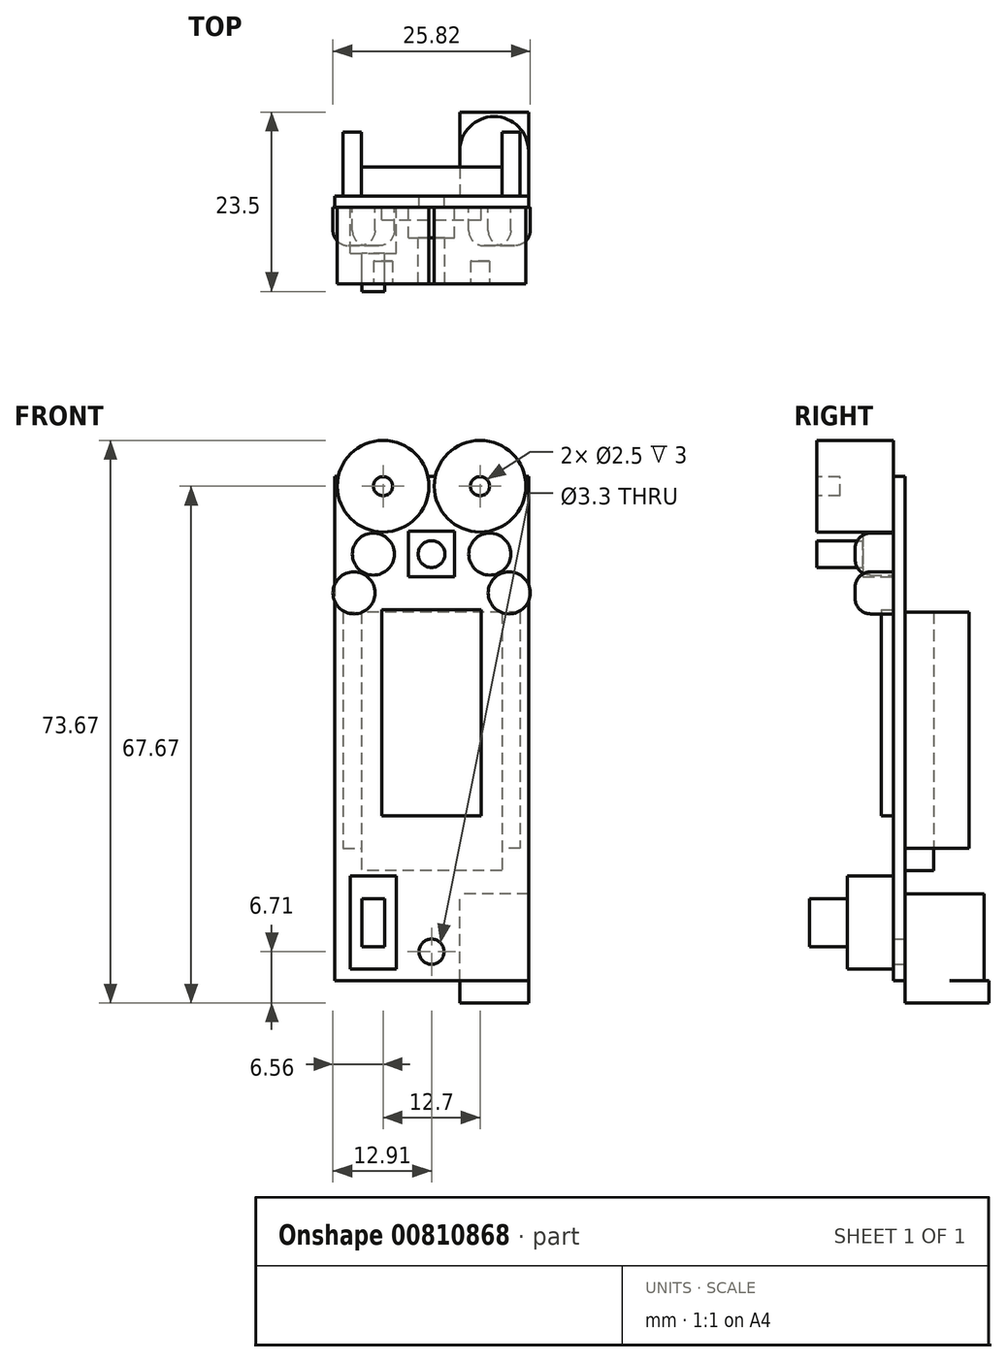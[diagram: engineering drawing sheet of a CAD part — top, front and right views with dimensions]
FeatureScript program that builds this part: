
annotation { "Feature Type Name" : "Feature", "Feature Type Description" : "" }
export const myFeature = defineFeature(function(context is Context, id is Id, definition is map)
    precondition{}
    {
        {
            var Q0;
            Q0=qCreatedBy(makeId("Front.planeOp"),FACE);
            var sketch = newSketch(context, id + "F0", { "sketchPlane" : qUnion([Q0])});
            skLineSegment(sketch, "E0.bottom", {"start": v(-12.7, 10.16) * mm, "end": v(12.7, 10.16) * mm});
            skLineSegment(sketch, "E0.top", {"start": v(-12.7, -55.88) * mm, "end": v(12.7, -55.88) * mm});
            skLineSegment(sketch, "E0.left", {"start": v(-12.7, 10.16) * mm, "end": v(-12.7, -55.88) * mm});
            skLineSegment(sketch, "E0.right", {"start": v(12.7, 10.16) * mm, "end": v(12.7, -55.88) * mm});
            skPoint(sketch, "E1", {"position": v(0, -52.07) * mm});
            skCircle(sketch, "E2", {"center": v(0, 2.54) * mm, "radius": 15.24 * mm, "construction": true});
            skCircle(sketch, "E3", {"center": v(-15.24, 13.97) * mm, "radius": 2.75 * mm, "construction": true});
            skCircle(sketch, "E4", {"center": v(15.24, 13.97) * mm, "radius": 2.75 * mm, "construction": true});
            skSolve(sketch);
        }
        {
            var Q0;
            Q0 = qSketchRegion(id + "F0", true);
            extrude(context, id + "F1", {"entities" : qUnion([Q0]), "depth" : 1.5 * mm, "offsetDistance" : 25.4 * mm});
        }
        {
            var Q0;
            Q0=sQuery(id+"F0.wireOp",VERTEX,"E1");
            var Q1;
            Q1=makeQuery(id+"F1.opExtrude","SWEPT_BODY",BODY,{"disambiguationData":[OSD([sQuery(id+"F0.wireOp",EDGE,"E0.bottom"),sQuery(id+"F0.wireOp",EDGE,"E0.top"),sQuery(id+"F0.wireOp",EDGE,"E0.left"),sQuery(id+"F0.wireOp",EDGE,"E0.right")])]});
            hole(context, id + "F2", {"style" : HoleStyle.SIMPLE, "endStyle" : HoleEndStyle.THROUGH, "oppositeDirection" : true, "standardTappedOrClearance" : lookupTablePath({ "standard" : "ISO", "fit" : "Normal", "size" : "M3", "type" : "Clearance" }), "standardBlindInLast" : lookupTablePath({ "fit" : "Standard", "standard" : "ISO", "size" : "M3", "type" : "Clearance" }), "holeDiameter" : 3.3 * mm, "majorDiameter" : 6.35 * mm, "isTappedThrough" : true, "tappedDepth" : 12.7 * mm, "tapClearance" : 3, "locations" : qUnion([Q0]), "scope" : qUnion([Q1])});
        }
        {
            var Q0;
            Q0=makeQuery(id+"F1.opExtrude","CAP_FACE",FACE,{"disambiguationData":[OSD([sQuery(id+"F0.wireOp",EDGE,"E0.bottom"),sQuery(id+"F0.wireOp",EDGE,"E0.top"),sQuery(id+"F0.wireOp",EDGE,"E0.left"),sQuery(id+"F0.wireOp",EDGE,"E0.right")])],"isStart":false});
            var sketch = newSketch(context, id + "F3", { "sketchPlane" : qUnion([Q0])});
            skCircle(sketch, "E5", {"center": v(-6.35, 8.9) * mm, "radius": 6 * mm});
            skCircle(sketch, "E6", {"center": v(6.35, 8.9) * mm, "radius": 6 * mm});
            skSolve(sketch);
        }
        {
            var Q0;
            Q0 = qSketchRegion(id + "F3", true);
            extrude(context, id + "F4", {"entities" : qUnion([Q0]), "depth" : 10 * mm, "offsetDistance" : 25.4 * mm});
        }
        {
            var Q0;
            Q0=makeQuery(id+"F1.opExtrude","CAP_FACE",FACE,{"disambiguationData":[OSD([sQuery(id+"F0.wireOp",EDGE,"E0.bottom"),sQuery(id+"F0.wireOp",EDGE,"E0.top"),sQuery(id+"F0.wireOp",EDGE,"E0.left"),sQuery(id+"F0.wireOp",EDGE,"E0.right")])],"isStart":false});
            var sketch = newSketch(context, id + "F5", { "sketchPlane" : qUnion([Q0])});
            skLineSegment(sketch, "E7.bottom", {"start": v(-3, 3) * mm, "end": v(3, 3) * mm});
            skLineSegment(sketch, "E7.top", {"start": v(-3, -3) * mm, "end": v(3, -3) * mm});
            skLineSegment(sketch, "E7.left", {"start": v(-3, 3) * mm, "end": v(-3, -3) * mm});
            skLineSegment(sketch, "E7.right", {"start": v(3, 3) * mm, "end": v(3, -3) * mm});
            skPoint(sketch, "E7.middle", {"position": v(0, 0) * mm});
            skSolve(sketch);
        }
        {
            var Q0;
            Q0 = qSketchRegion(id + "F5", true);
            extrude(context, id + "F6", {"entities" : qUnion([Q0]), "depth" : 4 * mm, "offsetDistance" : 25.4 * mm});
        }
        {
            var Q0;
            Q0=makeQuery(id+"F6.opExtrude","CAP_FACE",FACE,{"disambiguationData":[OSD([sQuery(id+"F5.wireOp",EDGE,"E7.bottom"),sQuery(id+"F5.wireOp",EDGE,"E7.top"),sQuery(id+"F5.wireOp",EDGE,"E7.left"),sQuery(id+"F5.wireOp",EDGE,"E7.right")])],"isStart":false});
            var sketch = newSketch(context, id + "F7", { "sketchPlane" : qUnion([Q0])});
            skCircle(sketch, "E8", {"center": v(0, 0) * mm, "radius": 1.75 * mm});
            skSolve(sketch);
        }
        {
            var Q0;
            Q0 = qSketchRegion(id + "F7", true);
            var Q1;
            Q1=makeQuery(id+"F4.opExtrude","CAP_FACE",FACE,{"disambiguationData":[OSD([sQuery(id+"F3.wireOp",EDGE,"E5")])],"isStart":false});
            extrude(context, id + "F8", {"entities" : qUnion([Q0]), "operationType" : NewBodyOperationType.ADD, "endBound" : BoundingType.UP_TO_SURFACE, "depth" : 25.4 * mm, "endBoundEntityFace" : qUnion([Q1]), "offsetDistance" : 25.4 * mm});
        }
        {
            var Q0;
            Q0=makeQuery(id+"F1.opExtrude","CAP_FACE",FACE,{"disambiguationData":[OSD([sQuery(id+"F0.wireOp",EDGE,"E0.bottom"),sQuery(id+"F0.wireOp",EDGE,"E0.top"),sQuery(id+"F0.wireOp",EDGE,"E0.left"),sQuery(id+"F0.wireOp",EDGE,"E0.right")])],"isStart":false});
            var sketch = newSketch(context, id + "F9", { "sketchPlane" : qUnion([Q0])});
            skCircle(sketch, "E9", {"center": v(-7.62, 0) * mm, "radius": 2.75 * mm});
            skCircle(sketch, "E10", {"center": v(-10.16, -5.08) * mm, "radius": 2.75 * mm});
            skCircle(sketch, "E11", {"center": v(7.62, 0) * mm, "radius": 2.75 * mm});
            skCircle(sketch, "E12", {"center": v(10.16, -5.08) * mm, "radius": 2.75 * mm});
            skSolve(sketch);
        }
        {
            var Q0;
            Q0 = qSketchRegion(id + "F9", true);
            extrude(context, id + "F10", {"entities" : qUnion([Q0]), "depth" : 5 * mm, "offsetDistance" : 25.4 * mm});
        }
        {
            var Q0;
            Q0=makeQuery(id+"F10.opExtrude","CAP_FACE",FACE,{"disambiguationData":[OSD([sQuery(id+"F9.wireOp",EDGE,"E10")])],"isStart":false});
            var Q1;
            Q1=makeQuery(id+"F10.opExtrude","CAP_FACE",FACE,{"disambiguationData":[OSD([sQuery(id+"F9.wireOp",EDGE,"E9")])],"isStart":false});
            var Q2;
            Q2=makeQuery(id+"F10.opExtrude","CAP_FACE",FACE,{"disambiguationData":[OSD([sQuery(id+"F9.wireOp",EDGE,"E11")])],"isStart":false});
            var Q3;
            Q3=makeQuery(id+"F10.opExtrude","CAP_FACE",FACE,{"disambiguationData":[OSD([sQuery(id+"F9.wireOp",EDGE,"E12")])],"isStart":false});
            fillet(context, id + "F11", {"entities" : qUnion([Q0, Q1, Q2, Q3]), "radius" : 2 * mm, "tangentPropagation" : true, "allowEdgeOverflow" : false});
        }
        {
            var Q0;
            Q0=makeQuery(id+"F1.opExtrude","CAP_FACE",FACE,{"disambiguationData":[OSD([sQuery(id+"F0.wireOp",EDGE,"E0.bottom"),sQuery(id+"F0.wireOp",EDGE,"E0.top"),sQuery(id+"F0.wireOp",EDGE,"E0.left"),sQuery(id+"F0.wireOp",EDGE,"E0.right")])],"isStart":false});
            var sketch = newSketch(context, id + "F12", { "sketchPlane" : qUnion([Q0])});
            skLineSegment(sketch, "E13.bottom", {"start": v(-6.5, -7.3) * mm, "end": v(6.5, -7.3) * mm});
            skLineSegment(sketch, "E13.top", {"start": v(-6.5, -34.3) * mm, "end": v(6.5, -34.3) * mm});
            skLineSegment(sketch, "E13.left", {"start": v(-6.5, -7.3) * mm, "end": v(-6.5, -34.3) * mm});
            skLineSegment(sketch, "E13.right", {"start": v(6.5, -7.3) * mm, "end": v(6.5, -34.3) * mm});
            skSolve(sketch);
        }
        {
            var Q0;
            Q0 = qSketchRegion(id + "F12", true);
            extrude(context, id + "F13", {"entities" : qUnion([Q0]), "depth" : 1.6 * mm, "offsetDistance" : 25.4 * mm});
        }
        {
            var Q0;
            Q0=makeQuery(id+"F1.opExtrude","CAP_FACE",FACE,{"disambiguationData":[OSD([sQuery(id+"F0.wireOp",EDGE,"E0.bottom"),sQuery(id+"F0.wireOp",EDGE,"E0.top"),sQuery(id+"F0.wireOp",EDGE,"E0.left"),sQuery(id+"F0.wireOp",EDGE,"E0.right")])],"isStart":false});
            var sketch = newSketch(context, id + "F14", { "sketchPlane" : qUnion([Q0])});
            skLineSegment(sketch, "E14.bottom", {"start": v(-10.62, -42.16) * mm, "end": v(-4.62, -42.16) * mm});
            skLineSegment(sketch, "E14.top", {"start": v(-10.62, -54.36) * mm, "end": v(-4.62, -54.36) * mm});
            skLineSegment(sketch, "E14.left", {"start": v(-10.62, -42.16) * mm, "end": v(-10.62, -54.36) * mm});
            skLineSegment(sketch, "E14.right", {"start": v(-4.62, -42.16) * mm, "end": v(-4.62, -54.36) * mm});
            skPoint(sketch, "E14.middle", {"position": v(-7.62, -48.26) * mm});
            skSolve(sketch);
        }
        {
            var Q0;
            Q0 = qSketchRegion(id + "F14", true);
            extrude(context, id + "F15", {"entities" : qUnion([Q0]), "depth" : 6 * mm, "offsetDistance" : 25.4 * mm});
        }
        {
            var Q0;
            Q0=makeQuery(id+"F15.opExtrude","CAP_FACE",FACE,{"disambiguationData":[OSD([sQuery(id+"F14.wireOp",EDGE,"E14.bottom"),sQuery(id+"F14.wireOp",EDGE,"E14.top"),sQuery(id+"F14.wireOp",EDGE,"E14.left"),sQuery(id+"F14.wireOp",EDGE,"E14.right")])],"isStart":false});
            var sketch = newSketch(context, id + "F16", { "sketchPlane" : qUnion([Q0])});
            skLineSegment(sketch, "E15.bottom", {"start": v(-6.12, -45.11) * mm, "end": v(-9.12, -45.11) * mm});
            skLineSegment(sketch, "E15.top", {"start": v(-6.12, -51.41) * mm, "end": v(-9.12, -51.41) * mm});
            skLineSegment(sketch, "E15.left", {"start": v(-6.12, -45.11) * mm, "end": v(-6.12, -51.41) * mm});
            skLineSegment(sketch, "E15.right", {"start": v(-9.12, -45.11) * mm, "end": v(-9.12, -51.41) * mm});
            skPoint(sketch, "E15.middle", {"position": v(-7.62, -48.26) * mm});
            skSolve(sketch);
        }
        {
            var Q0;
            Q0 = qSketchRegion(id + "F16", true);
            extrude(context, id + "F17", {"entities" : qUnion([Q0]), "operationType" : NewBodyOperationType.ADD, "depth" : 5 * mm, "offsetDistance" : 25.4 * mm});
        }
        {
            var Q0;
            Q0=qCreatedBy(makeId("Front.planeOp"),FACE);
            var sketch = newSketch(context, id + "F18", { "sketchPlane" : qUnion([Q0])});
            skLineSegment(sketch, "E16.bottom", {"start": v(9.2, -7.62) * mm, "end": v(-9.2, -7.62) * mm});
            skLineSegment(sketch, "E16.top", {"start": v(9.2, -41.42) * mm, "end": v(-9.2, -41.42) * mm});
            skLineSegment(sketch, "E16.left", {"start": v(9.2, -7.62) * mm, "end": v(9.2, -41.42) * mm});
            skLineSegment(sketch, "E16.right", {"start": v(-9.2, -7.62) * mm, "end": v(-9.2, -41.42) * mm});
            skSolve(sketch);
        }
        {
            var Q0;
            Q0 = qSketchRegion(id + "F18", true);
            extrude(context, id + "F19", {"entities" : qUnion([Q0]), "oppositeDirection" : true, "depth" : 3.8 * mm, "offsetDistance" : 25.4 * mm});
        }
        {
            var Q0;
            Q0=qCreatedBy(makeId("Front.planeOp"),FACE);
            var sketch = newSketch(context, id + "F20", { "sketchPlane" : qUnion([Q0])});
            skLineSegment(sketch, "E17.bottom", {"start": v(11.6, -7.62) * mm, "end": v(9.2, -7.62) * mm});
            skLineSegment(sketch, "E17.top", {"start": v(11.6, -38.52) * mm, "end": v(9.2, -38.52) * mm});
            skLineSegment(sketch, "E17.left", {"start": v(11.6, -7.62) * mm, "end": v(11.6, -38.52) * mm});
            skLineSegment(sketch, "E17.right", {"start": v(9.2, -7.62) * mm, "end": v(9.2, -38.52) * mm});
            skLineSegment(sketch, "E18.MirrorCS", {"start": v(-11.6, -7.62) * mm, "end": v(-9.2, -7.62) * mm});
            skLineSegment(sketch, "E19.MirrorCS", {"start": v(-9.2, -7.62) * mm, "end": v(-9.2, -38.52) * mm});
            skLineSegment(sketch, "E20.MirrorCS", {"start": v(-11.6, -38.52) * mm, "end": v(-9.2, -38.52) * mm});
            skLineSegment(sketch, "E21.MirrorCS", {"start": v(-11.6, -7.62) * mm, "end": v(-11.6, -38.52) * mm});
            skSolve(sketch);
        }
        {
            var Q0;
            Q0 = qSketchRegion(id + "F20", true);
            extrude(context, id + "F21", {"entities" : qUnion([Q0]), "oppositeDirection" : true, "depth" : 8.4 * mm, "offsetDistance" : 25.4 * mm});
        }
        {
            var Q0;
            Q0=qCreatedBy(makeId("Front.planeOp"),FACE);
            var sketch = newSketch(context, id + "F22", { "sketchPlane" : qUnion([Q0])});
            skLineSegment(sketch, "E22.bottom", {"start": v(12.7, -44.48) * mm, "end": v(3.7, -44.48) * mm});
            skLineSegment(sketch, "E22.top", {"start": v(12.7, -58.78) * mm, "end": v(3.7, -58.78) * mm});
            skLineSegment(sketch, "E22.left", {"start": v(12.7, -44.48) * mm, "end": v(12.7, -58.78) * mm});
            skLineSegment(sketch, "E22.right", {"start": v(3.7, -44.48) * mm, "end": v(3.7, -58.78) * mm});
            skSolve(sketch);
        }
        {
            var Q0;
            Q0 = qSketchRegion(id + "F22", true);
            extrude(context, id + "F23", {"entities" : qUnion([Q0]), "oppositeDirection" : true, "depth" : 11 * mm, "offsetDistance" : 25.4 * mm});
        }
        {
            var Q0;
            Q0=makeQuery(id+"F23.opExtrude","SWEPT_FACE",FACE,{"disambiguationData":[OSD([sQuery(id+"F22.wireOp",EDGE,"E22.bottom")])]});
            var sketch = newSketch(context, id + "F24", { "sketchPlane" : qUnion([Q0])});
            skArc(sketch, "E23", {"start": v(12.7, 5.9) * mm, "mid": v(8.2, 10.4) * mm, "end": v(3.7, 5.9) * mm});
            skSolve(sketch);
        }
        {
            var Q0;
            {var subQ0=sQuery(id+"F24.wireOp",EDGE,"E23");Q0=makeQuery(id+"F24.imprint","IMPRINT",FACE,{"disambiguationData":[TD([[makeQuery(id+"F24.imprint","IMPRINT",EDGE,{"derivedFrom":subQ0}),-1.0]])]});}
            var Q1;
            Q1=makeQuery(id+"F1.opExtrude","SWEPT_FACE",FACE,{"disambiguationData":[OSD([sQuery(id+"F0.wireOp",EDGE,"E0.top")])]});
            extrude(context, id + "F25", {"entities" : qUnion([Q0]), "operationType" : NewBodyOperationType.REMOVE, "endBound" : BoundingType.UP_TO_SURFACE, "oppositeDirection" : true, "depth" : 25.4 * mm, "endBoundEntityFace" : qUnion([Q1]), "offsetDistance" : 25.4 * mm});
        }
        {
            var Q0;
            Q0=makeQuery(id+"F4.opExtrude","CAP_FACE",FACE,{"disambiguationData":[OSD([sQuery(id+"F3.wireOp",EDGE,"E5")])],"isStart":false});
            var sketch = newSketch(context, id + "F26", { "sketchPlane" : qUnion([Q0])});
            skCircle(sketch, "E24", {"center": v(-6.35, 8.9) * mm, "radius": 1.25 * mm});
            skCircle(sketch, "E25", {"center": v(6.35, 8.9) * mm, "radius": 1.25 * mm});
            skSolve(sketch);
        }
        {
            var Q0;
            Q0 = qSketchRegion(id + "F26", true);
            extrude(context, id + "F27", {"entities" : qUnion([Q0]), "operationType" : NewBodyOperationType.REMOVE, "oppositeDirection" : true, "depth" : 3 * mm, "offsetDistance" : 25.4 * mm});
        }
    });
